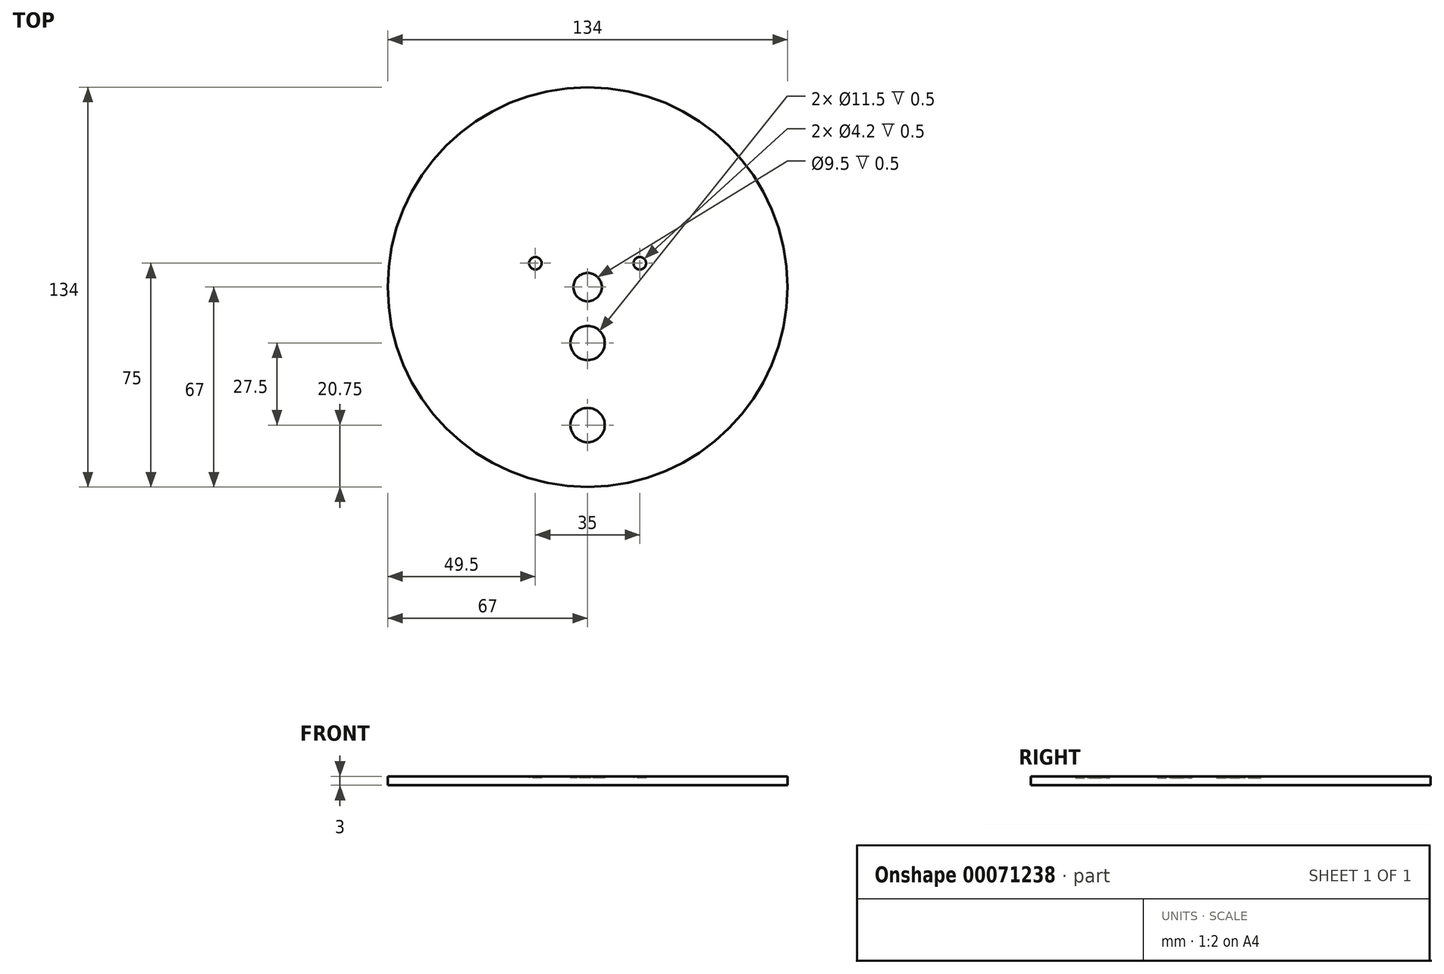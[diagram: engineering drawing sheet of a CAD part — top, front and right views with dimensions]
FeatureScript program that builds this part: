
annotation { "Feature Type Name" : "Feature", "Feature Type Description" : "" }
export const myFeature = defineFeature(function(context is Context, id is Id, definition is map)
    precondition{}
    {
        {
            var Q0;
            Q0=qCreatedBy(makeId("Top.planeOp"),FACE);
            var sketch = newSketch(context, id + "F0", { "sketchPlane" : qUnion([Q0])});
            skCircle(sketch, "E0", {"center": v(0, 0) * mm, "radius": 67 * mm});
            skSolve(sketch);
        }
        {
            var Q0;
            Q0=makeQuery(id+"F0.imprint","IMPRINT",FACE,{"disambiguationData":[TD([[makeQuery(id+"F0.imprint","IMPRINT",EDGE,{"derivedFrom":sQuery(id+"F0.wireOp",EDGE,"E0")}),1.0]])]});
            extrude(context, id + "F1", {"entities" : qUnion([Q0]), "endBound" : BoundingType.SYMMETRIC, "depth" : 5 * mm});
        }
        {
            var Q0;
            Q0=qCreatedBy(makeId("Top.planeOp"),FACE);
            var sketch = newSketch(context, id + "F2", { "sketchPlane" : qUnion([Q0])});
            skCircle(sketch, "E1", {"center": v(0, 0) * mm, "radius": 58.88 * mm});
            skCircle(sketch, "E2", {"center": v(0, 0) * mm, "radius": 62.62 * mm});
            skCircle(sketch, "E3", {"center": v(0, 0) * mm, "radius": 64.38 * mm});
            skSolve(sketch);
        }
        {
            var Q0;
            Q0=sQuery(id+"F2.wireOp",EDGE,"E3");
            extrude(context, id + "F3", {"bodyType" : ToolBodyType.SURFACE, "surfaceEntities" : qUnion([Q0]), "depth" : 3 * mm});
        }
        {
            var Q0;
            Q0=makeQuery(id+"F1.opExtrude","CAP_FACE",FACE,{"disambiguationData":[OSD([sQuery(id+"F0.wireOp",EDGE,"E0")])],"isStart":false});
            var Q1;
            Q1=sQuery(id+"F2.wireOp",EDGE,"E2");
            var Q2;
            Q2=sQuery(id+"F2.wireOp",EDGE,"E3");
            extrude(context, id + "F4", {"entities" : qUnion([Q0]), "operationType" : NewBodyOperationType.REMOVE, "surfaceEntities" : qUnion([Q1, Q2]), "oppositeDirection" : true, "depth" : 2 * mm});
        }
        {
            var Q0;
            Q0=qCreatedBy(makeId("Top.planeOp"),FACE);
            var sketch = newSketch(context, id + "F5", { "sketchPlane" : qUnion([Q0])});
            skCircle(sketch, "E4", {"center": v(0, 0) * mm, "radius": 4.75 * mm});
            skCircle(sketch, "E5", {"center": v(0, -18.75) * mm, "radius": 5.75 * mm});
            skCircle(sketch, "E6", {"center": v(0, -46.25) * mm, "radius": 5.75 * mm});
            skSolve(sketch);
        }
        {
            var Q0;
            Q0=qCreatedBy(makeId("Top.planeOp"),FACE);
            var sketch = newSketch(context, id + "F6", { "sketchPlane" : qUnion([Q0])});
            skLineSegment(sketch, "E7", {"start": v(0, 8) * mm, "end": v(17.5, 8) * mm, "construction": true});
            skCircle(sketch, "E8", {"center": v(17.5, 8) * mm, "radius": 2.1 * mm});
            skLineSegment(sketch, "E9", {"start": v(0, 0) * mm, "end": v(0, 8) * mm, "construction": true});
            skCircle(sketch, "E10.MirrorC", {"center": v(-17.5, 8) * mm, "radius": 2.1 * mm});
            skSolve(sketch);
        }
        {
            var Q0;
            Q0 = qSketchRegion(id + "F6", true);
            var Q1;
            Q1 = qSketchRegion(id + "F5", true);
            var Q2;
            Q2=sQuery(id+"F5.wireOp",EDGE,"E6");
            var Q3;
            Q3=sQuery(id+"F5.wireOp",EDGE,"E5");
            var Q4;
            Q4=sQuery(id+"F5.wireOp",EDGE,"E4");
            var Q5;
            Q5=sQuery(id+"F6.wireOp",EDGE,"E10.MirrorC");
            var Q6;
            Q6=sQuery(id+"F6.wireOp",EDGE,"E8");
            extrude(context, id + "F7", {"entities" : qUnion([Q0, Q1]), "operationType" : NewBodyOperationType.REMOVE, "surfaceEntities" : qUnion([Q2, Q3, Q4, Q5, Q6]), "endBound" : BoundingType.THROUGH_ALL, "depth" : 25.4 * mm});
        }
    });
